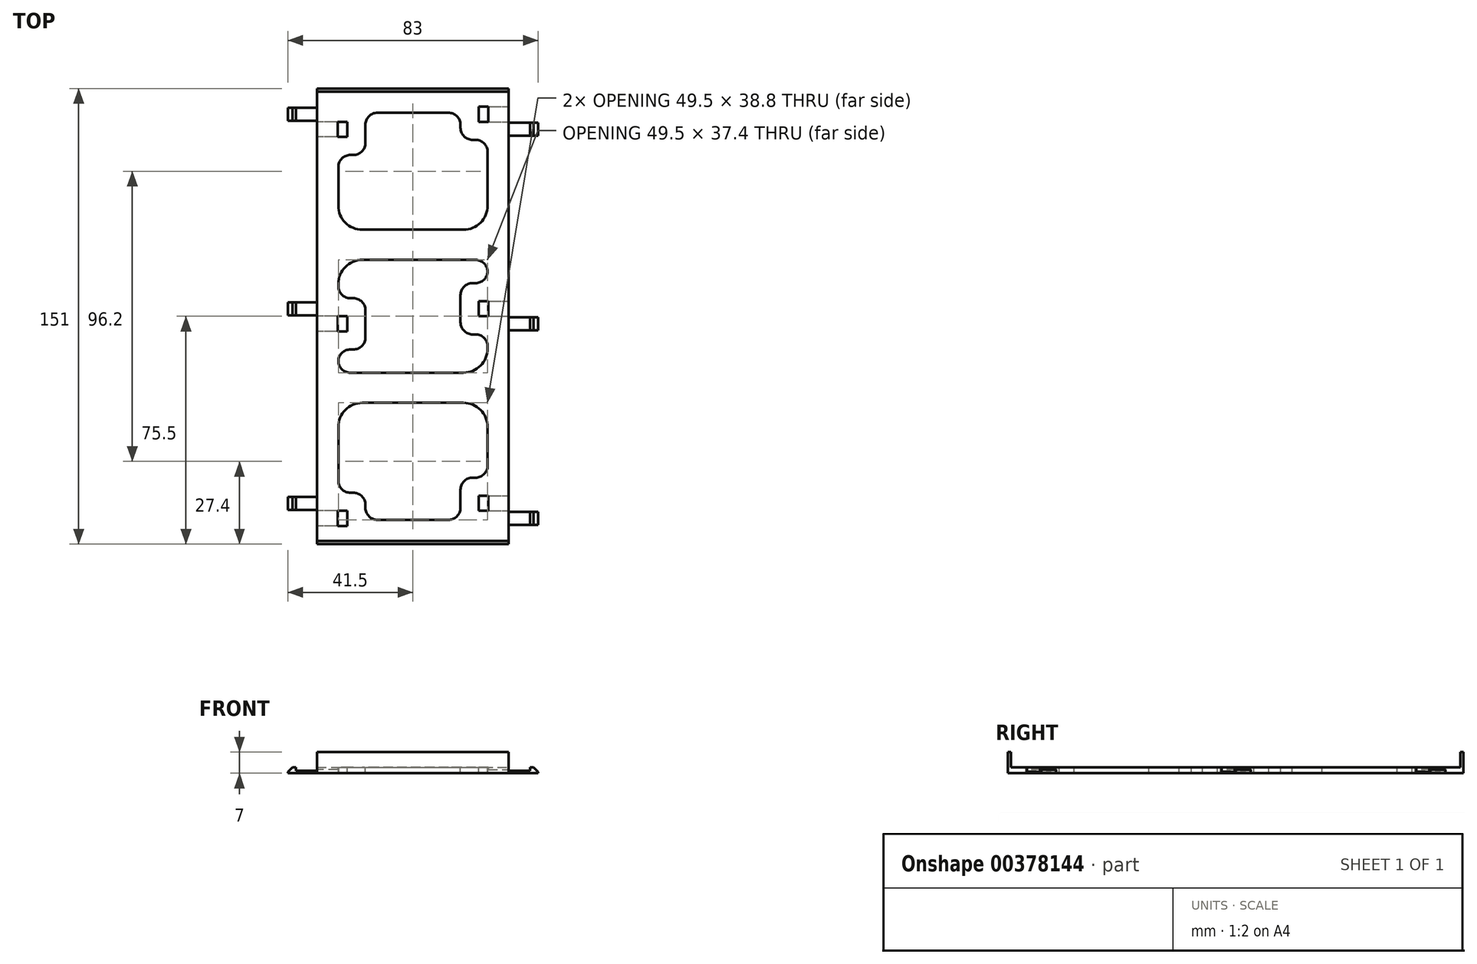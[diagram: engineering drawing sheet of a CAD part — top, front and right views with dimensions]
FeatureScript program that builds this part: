
annotation { "Feature Type Name" : "Feature", "Feature Type Description" : "" }
export const myFeature = defineFeature(function(context is Context, id is Id, definition is map)
    precondition{}
    {
        {
            var Q0;
            Q0=qCreatedBy(makeId("Top.planeOp"),FACE);
            var sketch = newSketch(context, id + "F0", { "sketchPlane" : qUnion([Q0])});
            skLineSegment(sketch, "E0.bottom", {"start": v(0, 0) * mm, "end": v(63.5, 0) * mm});
            skLineSegment(sketch, "E0.top", {"start": v(0, 151) * mm, "end": v(63.5, 151) * mm});
            skLineSegment(sketch, "E0.left", {"start": v(0, 0) * mm, "end": v(0, 151) * mm});
            skLineSegment(sketch, "E0.right", {"start": v(63.5, 0) * mm, "end": v(63.5, 151) * mm});
            skSolve(sketch);
        }
        {
            var Q0;
            Q0=makeQuery(id+"F0.imprint","IMPRINT",FACE,{"disambiguationData":[TD([[makeQuery(id+"F0.imprint","IMPRINT",EDGE,{"derivedFrom":sQuery(id+"F0.wireOp",EDGE,"E0.bottom")}),1.0]])]});
            extrude(context, id + "F1", {"entities" : qUnion([Q0]), "depth" : 2 * mm});
        }
        {
            var Q0;
            Q0=makeQuery(id+"F1.opExtrude","CAP_FACE",FACE,{"disambiguationData":[OSD([sQuery(id+"F0.wireOp",EDGE,"E0.bottom"),sQuery(id+"F0.wireOp",EDGE,"E0.top"),sQuery(id+"F0.wireOp",EDGE,"E0.left"),sQuery(id+"F0.wireOp",EDGE,"E0.right")])],"isStart":false});
            var sketch = newSketch(context, id + "F2", { "sketchPlane" : qUnion([Q0])});
            skLineSegment(sketch, "E1.bottom", {"start": v(0, 151) * mm, "end": v(63.5, 151) * mm});
            skLineSegment(sketch, "E1.top", {"start": v(0, 150) * mm, "end": v(63.5, 150) * mm});
            skLineSegment(sketch, "E1.left", {"start": v(0, 151) * mm, "end": v(0, 150) * mm});
            skLineSegment(sketch, "E1.right", {"start": v(63.5, 151) * mm, "end": v(63.5, 150) * mm});
            skLineSegment(sketch, "E2.bottom", {"start": v(0, 0) * mm, "end": v(63.5, 0) * mm});
            skLineSegment(sketch, "E2.top", {"start": v(0, 1) * mm, "end": v(63.5, 1) * mm});
            skLineSegment(sketch, "E2.left", {"start": v(0, 0) * mm, "end": v(0, 1) * mm});
            skLineSegment(sketch, "E2.right", {"start": v(63.5, 0) * mm, "end": v(63.5, 1) * mm});
            skSolve(sketch);
        }
        {
            var Q0;
            Q0=makeQuery(id+"F2.imprint","IMPRINT",FACE,{"disambiguationData":[TD([[makeQuery(id+"F2.imprint","IMPRINT",EDGE,{"derivedFrom":sQuery(id+"F2.wireOp",EDGE,"E2.bottom")}),1.0]])]});
            var Q1;
            Q1=makeQuery(id+"F2.imprint","IMPRINT",FACE,{"disambiguationData":[TD([[makeQuery(id+"F2.imprint","IMPRINT",EDGE,{"derivedFrom":sQuery(id+"F2.wireOp",EDGE,"E1.bottom")}),-1.0]])]});
            extrude(context, id + "F3", {"entities" : qUnion([Q0, Q1]), "operationType" : NewBodyOperationType.ADD, "depth" : 5 * mm});
        }
        {
            var Q0;
            Q0=makeQuery(id+"F3.boolean.opBoolean","MERGE",FACE,{"derivedFrom":[makeQuery(id+"F1.opExtrude","SWEPT_FACE",FACE,{"disambiguationData":[OSD([sQuery(id+"F0.wireOp",EDGE,"E0.right")])]}),makeQuery(id+"F3.opExtrude","SWEPT_FACE",FACE,{"disambiguationData":[OSD([sQuery(id+"F2.wireOp",EDGE,"E1.right")])]}),makeQuery(id+"F3.opExtrude","SWEPT_FACE",FACE,{"disambiguationData":[OSD([sQuery(id+"F2.wireOp",EDGE,"E2.right")])]})]});
            var sketch = newSketch(context, id + "F4", { "sketchPlane" : qUnion([Q0])});
            skLineSegment(sketch, "E3.bottom", {"start": v(11, 0) * mm, "end": v(16, 0) * mm});
            skLineSegment(sketch, "E3.top", {"start": v(11, 1.2) * mm, "end": v(16, 1.2) * mm});
            skLineSegment(sketch, "E3.left", {"start": v(11, 0) * mm, "end": v(11, 1.2) * mm});
            skLineSegment(sketch, "E3.right", {"start": v(16, 0) * mm, "end": v(16, 1.2) * mm});
            skLineSegment(sketch, "E4.bottom", {"start": v(75.5, 0) * mm, "end": v(80.5, 0) * mm});
            skLineSegment(sketch, "E4.top", {"start": v(75.5, 1.2) * mm, "end": v(80.5, 1.2) * mm});
            skLineSegment(sketch, "E4.left", {"start": v(75.5, 0) * mm, "end": v(75.5, 1.2) * mm});
            skLineSegment(sketch, "E4.right", {"start": v(80.5, 0) * mm, "end": v(80.5, 1.2) * mm});
            skLineSegment(sketch, "E5.bottom", {"start": v(140, 0) * mm, "end": v(145, 0) * mm});
            skLineSegment(sketch, "E5.top", {"start": v(140, 1.2) * mm, "end": v(145, 1.2) * mm});
            skLineSegment(sketch, "E5.left", {"start": v(140, 0) * mm, "end": v(140, 1.2) * mm});
            skLineSegment(sketch, "E5.right", {"start": v(145, 0) * mm, "end": v(145, 1.2) * mm});
            skSolve(sketch);
        }
        {
            var Q0;
            Q0=makeQuery(id+"F4.imprint","IMPRINT",FACE,{"disambiguationData":[TD([[makeQuery(id+"F4.imprint","IMPRINT",EDGE,{"derivedFrom":sQuery(id+"F4.wireOp",EDGE,"E3.bottom")}),1.0]])]});
            var Q1;
            Q1=makeQuery(id+"F4.imprint","IMPRINT",FACE,{"disambiguationData":[TD([[makeQuery(id+"F4.imprint","IMPRINT",EDGE,{"derivedFrom":sQuery(id+"F4.wireOp",EDGE,"E4.bottom")}),1.0]])]});
            var Q2;
            Q2=makeQuery(id+"F4.imprint","IMPRINT",FACE,{"disambiguationData":[TD([[makeQuery(id+"F4.imprint","IMPRINT",EDGE,{"derivedFrom":sQuery(id+"F4.wireOp",EDGE,"E5.bottom")}),1.0]])]});
            extrude(context, id + "F5", {"entities" : qUnion([Q0, Q1, Q2]), "operationType" : NewBodyOperationType.REMOVE, "oppositeDirection" : true, "depth" : 10 * mm});
        }
        {
            var Q0;
            Q0=makeQuery(id+"F3.boolean.opBoolean","MERGE",FACE,{"derivedFrom":[makeQuery(id+"F1.opExtrude","SWEPT_FACE",FACE,{"disambiguationData":[OSD([sQuery(id+"F0.wireOp",EDGE,"E0.left")])]}),makeQuery(id+"F3.opExtrude","SWEPT_FACE",FACE,{"disambiguationData":[OSD([sQuery(id+"F2.wireOp",EDGE,"E1.left")])]}),makeQuery(id+"F3.opExtrude","SWEPT_FACE",FACE,{"disambiguationData":[OSD([sQuery(id+"F2.wireOp",EDGE,"E2.left")])]})]});
            var sketch = newSketch(context, id + "F6", { "sketchPlane" : qUnion([Q0])});
            skLineSegment(sketch, "E6.bottom", {"start": v(-140, 0) * mm, "end": v(-135, 0) * mm});
            skLineSegment(sketch, "E6.top", {"start": v(-140, 1.2) * mm, "end": v(-135, 1.2) * mm});
            skLineSegment(sketch, "E6.left", {"start": v(-140, 0) * mm, "end": v(-140, 1.2) * mm});
            skLineSegment(sketch, "E6.right", {"start": v(-135, 0) * mm, "end": v(-135, 1.2) * mm});
            skLineSegment(sketch, "E7.bottom", {"start": v(-75.5, 0) * mm, "end": v(-70.5, 0) * mm});
            skLineSegment(sketch, "E7.top", {"start": v(-75.5, 1.2) * mm, "end": v(-70.5, 1.2) * mm});
            skLineSegment(sketch, "E7.left", {"start": v(-75.5, 0) * mm, "end": v(-75.5, 1.2) * mm});
            skLineSegment(sketch, "E7.right", {"start": v(-70.5, 0) * mm, "end": v(-70.5, 1.2) * mm});
            skLineSegment(sketch, "E8.bottom", {"start": v(-11, 0) * mm, "end": v(-6, 0) * mm});
            skLineSegment(sketch, "E8.top", {"start": v(-11, 1.2) * mm, "end": v(-6, 1.2) * mm});
            skLineSegment(sketch, "E8.left", {"start": v(-11, 0) * mm, "end": v(-11, 1.2) * mm});
            skLineSegment(sketch, "E8.right", {"start": v(-6, 0) * mm, "end": v(-6, 1.2) * mm});
            skSolve(sketch);
        }
        {
            var Q0;
            Q0=makeQuery(id+"F6.imprint","IMPRINT",FACE,{"disambiguationData":[TD([[makeQuery(id+"F6.imprint","IMPRINT",EDGE,{"derivedFrom":sQuery(id+"F6.wireOp",EDGE,"E6.bottom")}),-1.0]])]});
            var Q1;
            Q1=makeQuery(id+"F6.imprint","IMPRINT",FACE,{"disambiguationData":[TD([[makeQuery(id+"F6.imprint","IMPRINT",EDGE,{"derivedFrom":sQuery(id+"F6.wireOp",EDGE,"E7.bottom")}),-1.0]])]});
            var Q2;
            Q2=makeQuery(id+"F6.imprint","IMPRINT",FACE,{"disambiguationData":[TD([[makeQuery(id+"F6.imprint","IMPRINT",EDGE,{"derivedFrom":sQuery(id+"F6.wireOp",EDGE,"E8.bottom")}),-1.0]])]});
            extrude(context, id + "F7", {"entities" : qUnion([Q0, Q1, Q2]), "operationType" : NewBodyOperationType.REMOVE, "oppositeDirection" : true, "depth" : 10 * mm});
        }
        {
            var Q0;
            Q0=makeQuery(id+"F3.boolean.opBoolean","MERGE",FACE,{"derivedFrom":[makeQuery(id+"F1.opExtrude","SWEPT_FACE",FACE,{"disambiguationData":[OSD([sQuery(id+"F0.wireOp",EDGE,"E0.right")])]}),makeQuery(id+"F3.opExtrude","SWEPT_FACE",FACE,{"disambiguationData":[OSD([sQuery(id+"F2.wireOp",EDGE,"E1.right")])]}),makeQuery(id+"F3.opExtrude","SWEPT_FACE",FACE,{"disambiguationData":[OSD([sQuery(id+"F2.wireOp",EDGE,"E2.right")])]})]});
            var sketch = newSketch(context, id + "F8", { "sketchPlane" : qUnion([Q0])});
            skLineSegment(sketch, "E9.bottom", {"start": v(6.35, 0.8) * mm, "end": v(10.65, 0.8) * mm});
            skLineSegment(sketch, "E9.top", {"start": v(6.35, 0) * mm, "end": v(10.65, 0) * mm});
            skLineSegment(sketch, "E9.left", {"start": v(6.35, 0.8) * mm, "end": v(6.35, 0) * mm});
            skLineSegment(sketch, "E9.right", {"start": v(10.65, 0.8) * mm, "end": v(10.65, 0) * mm});
            skLineSegment(sketch, "E10.bottom", {"start": v(70.85, 0.8) * mm, "end": v(75.15, 0.8) * mm});
            skLineSegment(sketch, "E10.top", {"start": v(70.85, 0) * mm, "end": v(75.15, 0) * mm});
            skLineSegment(sketch, "E10.left", {"start": v(70.85, 0.8) * mm, "end": v(70.85, 0) * mm});
            skLineSegment(sketch, "E10.right", {"start": v(75.15, 0.8) * mm, "end": v(75.15, 0) * mm});
            skLineSegment(sketch, "E11.bottom", {"start": v(135.35, 0.8) * mm, "end": v(139.65, 0.8) * mm});
            skLineSegment(sketch, "E11.top", {"start": v(135.35, 0) * mm, "end": v(139.65, 0) * mm});
            skLineSegment(sketch, "E11.left", {"start": v(135.35, 0.8) * mm, "end": v(135.35, 0) * mm});
            skLineSegment(sketch, "E11.right", {"start": v(139.65, 0.8) * mm, "end": v(139.65, 0) * mm});
            skSolve(sketch);
        }
        {
            var Q0;
            Q0=makeQuery(id+"F8.imprint","IMPRINT",FACE,{"disambiguationData":[TD([[makeQuery(id+"F8.imprint","IMPRINT",EDGE,{"derivedFrom":sQuery(id+"F8.wireOp",EDGE,"E11.bottom")}),-1.0]])]});
            var Q1;
            Q1=makeQuery(id+"F8.imprint","IMPRINT",FACE,{"disambiguationData":[TD([[makeQuery(id+"F8.imprint","IMPRINT",EDGE,{"derivedFrom":sQuery(id+"F8.wireOp",EDGE,"E10.bottom")}),-1.0]])]});
            var Q2;
            Q2=makeQuery(id+"F8.imprint","IMPRINT",FACE,{"disambiguationData":[TD([[makeQuery(id+"F8.imprint","IMPRINT",EDGE,{"derivedFrom":sQuery(id+"F8.wireOp",EDGE,"E9.bottom")}),-1.0]])]});
            extrude(context, id + "F9", {"entities" : qUnion([Q0, Q1, Q2]), "operationType" : NewBodyOperationType.ADD, "depth" : 9.75 * mm});
        }
        {
            var Q0;
            Q0=makeQuery(id+"F3.boolean.opBoolean","MERGE",FACE,{"derivedFrom":[makeQuery(id+"F1.opExtrude","SWEPT_FACE",FACE,{"disambiguationData":[OSD([sQuery(id+"F0.wireOp",EDGE,"E0.left")])]}),makeQuery(id+"F3.opExtrude","SWEPT_FACE",FACE,{"disambiguationData":[OSD([sQuery(id+"F2.wireOp",EDGE,"E1.left")])]}),makeQuery(id+"F3.opExtrude","SWEPT_FACE",FACE,{"disambiguationData":[OSD([sQuery(id+"F2.wireOp",EDGE,"E2.left")])]})]});
            var sketch = newSketch(context, id + "F10", { "sketchPlane" : qUnion([Q0])});
            skPoint(sketch, "E12.firstSnap0", {"position": v(-144.65, 0) * mm});
            skLineSegment(sketch, "E12.bottom", {"start": v(-144.65, 0.8) * mm, "end": v(-140.35, 0.8) * mm});
            skLineSegment(sketch, "E12.top", {"start": v(-144.65, 0) * mm, "end": v(-140.35, 0) * mm});
            skLineSegment(sketch, "E12.left", {"start": v(-144.65, 0.8) * mm, "end": v(-144.65, 0) * mm});
            skLineSegment(sketch, "E12.right", {"start": v(-140.35, 0.8) * mm, "end": v(-140.35, 0) * mm});
            skLineSegment(sketch, "E13.bottom", {"start": v(-80.15, 0.8) * mm, "end": v(-75.85, 0.8) * mm});
            skLineSegment(sketch, "E13.top", {"start": v(-80.15, 0) * mm, "end": v(-75.85, 0) * mm});
            skLineSegment(sketch, "E13.left", {"start": v(-80.15, 0.8) * mm, "end": v(-80.15, 0) * mm});
            skLineSegment(sketch, "E13.right", {"start": v(-75.85, 0.8) * mm, "end": v(-75.85, 0) * mm});
            skLineSegment(sketch, "E14.bottom", {"start": v(-15.65, 0.8) * mm, "end": v(-11.35, 0.8) * mm});
            skLineSegment(sketch, "E14.top", {"start": v(-15.65, 0) * mm, "end": v(-11.35, 0) * mm});
            skLineSegment(sketch, "E14.left", {"start": v(-15.65, 0.8) * mm, "end": v(-15.65, 0) * mm});
            skLineSegment(sketch, "E14.right", {"start": v(-11.35, 0.8) * mm, "end": v(-11.35, 0) * mm});
            skSolve(sketch);
        }
        {
            var Q0;
            Q0=makeQuery(id+"F10.imprint","IMPRINT",FACE,{"disambiguationData":[TD([[makeQuery(id+"F10.imprint","IMPRINT",EDGE,{"derivedFrom":sQuery(id+"F10.wireOp",EDGE,"E14.bottom")}),-1.0]])]});
            var Q1;
            Q1=makeQuery(id+"F10.imprint","IMPRINT",FACE,{"disambiguationData":[TD([[makeQuery(id+"F10.imprint","IMPRINT",EDGE,{"derivedFrom":sQuery(id+"F10.wireOp",EDGE,"E13.bottom")}),-1.0]])]});
            var Q2;
            Q2=makeQuery(id+"F10.imprint","IMPRINT",FACE,{"disambiguationData":[TD([[makeQuery(id+"F10.imprint","IMPRINT",EDGE,{"derivedFrom":sQuery(id+"F10.wireOp",EDGE,"E12.bottom")}),-1.0]])]});
            extrude(context, id + "F11", {"entities" : qUnion([Q0, Q1, Q2]), "operationType" : NewBodyOperationType.ADD, "depth" : 9.75 * mm});
        }
        {
            var Q0;
            Q0=makeQuery(id+"F9.opExtrude","SWEPT_FACE",FACE,{"disambiguationData":[OSD([sQuery(id+"F8.wireOp",EDGE,"E9.bottom")])]});
            var sketch = newSketch(context, id + "F12", { "sketchPlane" : qUnion([Q0])});
            skLineSegment(sketch, "E15.bottom", {"start": v(73.25, 6.35) * mm, "end": v(70.5, 6.35) * mm});
            skLineSegment(sketch, "E15.top", {"start": v(73.25, 10.65) * mm, "end": v(70.5, 10.65) * mm});
            skLineSegment(sketch, "E15.left", {"start": v(73.25, 6.35) * mm, "end": v(73.25, 10.65) * mm});
            skLineSegment(sketch, "E15.right", {"start": v(70.5, 6.35) * mm, "end": v(70.5, 10.65) * mm});
            skSolve(sketch);
        }
        {
            var Q0;
            Q0=makeQuery(id+"F12.imprint","IMPRINT",FACE,{"disambiguationData":[TD([[makeQuery(id+"F12.imprint","IMPRINT",EDGE,{"derivedFrom":sQuery(id+"F12.wireOp",EDGE,"E15.bottom")}),-1.0]])]});
            extrude(context, id + "F13", {"entities" : qUnion([Q0]), "operationType" : NewBodyOperationType.ADD, "depth" : 1.2 * mm});
        }
        {
            var Q0;
            Q0=makeQuery(id+"F11.opExtrude","SWEPT_FACE",FACE,{"disambiguationData":[OSD([sQuery(id+"F10.wireOp",EDGE,"E14.bottom")])]});
            var sketch = newSketch(context, id + "F14", { "sketchPlane" : qUnion([Q0])});
            skLineSegment(sketch, "E16.bottom", {"start": v(-9.75, 15.65) * mm, "end": v(-7, 15.65) * mm});
            skLineSegment(sketch, "E16.top", {"start": v(-9.75, 11.35) * mm, "end": v(-7, 11.35) * mm});
            skLineSegment(sketch, "E16.left", {"start": v(-9.75, 15.65) * mm, "end": v(-9.75, 11.35) * mm});
            skLineSegment(sketch, "E16.right", {"start": v(-7, 15.65) * mm, "end": v(-7, 11.35) * mm});
            skSolve(sketch);
        }
        {
            var Q0;
            Q0=makeQuery(id+"F14.imprint","IMPRINT",FACE,{"disambiguationData":[TD([[makeQuery(id+"F14.imprint","IMPRINT",EDGE,{"derivedFrom":sQuery(id+"F14.wireOp",EDGE,"E16.bottom")}),-1.0]])]});
            extrude(context, id + "F15", {"entities" : qUnion([Q0]), "operationType" : NewBodyOperationType.ADD, "depth" : 1.2 * mm});
        }
        {
            var Q0;
            Q0=makeQuery(id+"F9.opExtrude","SWEPT_FACE",FACE,{"disambiguationData":[OSD([sQuery(id+"F8.wireOp",EDGE,"E10.bottom")])]});
            var sketch = newSketch(context, id + "F16", { "sketchPlane" : qUnion([Q0])});
            skLineSegment(sketch, "E17.bottom", {"start": v(73.25, 75.15) * mm, "end": v(70.5, 75.15) * mm});
            skLineSegment(sketch, "E17.top", {"start": v(73.25, 70.85) * mm, "end": v(70.5, 70.85) * mm});
            skLineSegment(sketch, "E17.left", {"start": v(73.25, 75.15) * mm, "end": v(73.25, 70.85) * mm});
            skLineSegment(sketch, "E17.right", {"start": v(70.5, 75.15) * mm, "end": v(70.5, 70.85) * mm});
            skSolve(sketch);
        }
        {
            var Q0;
            Q0=makeQuery(id+"F16.imprint","IMPRINT",FACE,{"disambiguationData":[TD([[makeQuery(id+"F16.imprint","IMPRINT",EDGE,{"derivedFrom":sQuery(id+"F16.wireOp",EDGE,"E17.bottom")}),1.0]])]});
            extrude(context, id + "F17", {"entities" : qUnion([Q0]), "operationType" : NewBodyOperationType.ADD, "depth" : 1.2 * mm});
        }
        {
            var Q0;
            Q0=makeQuery(id+"F11.opExtrude","SWEPT_FACE",FACE,{"disambiguationData":[OSD([sQuery(id+"F10.wireOp",EDGE,"E13.bottom")])]});
            var sketch = newSketch(context, id + "F18", { "sketchPlane" : qUnion([Q0])});
            skLineSegment(sketch, "E18.bottom", {"start": v(-9.75, 80.15) * mm, "end": v(-7, 80.15) * mm});
            skLineSegment(sketch, "E18.top", {"start": v(-9.75, 75.85) * mm, "end": v(-7, 75.85) * mm});
            skLineSegment(sketch, "E18.left", {"start": v(-9.75, 80.15) * mm, "end": v(-9.75, 75.85) * mm});
            skLineSegment(sketch, "E18.right", {"start": v(-7, 80.15) * mm, "end": v(-7, 75.85) * mm});
            skSolve(sketch);
        }
        {
            var Q0;
            Q0=makeQuery(id+"F18.imprint","IMPRINT",FACE,{"disambiguationData":[TD([[makeQuery(id+"F18.imprint","IMPRINT",EDGE,{"derivedFrom":sQuery(id+"F18.wireOp",EDGE,"E18.bottom")}),-1.0]])]});
            extrude(context, id + "F19", {"entities" : qUnion([Q0]), "operationType" : NewBodyOperationType.ADD, "depth" : 1.2 * mm});
        }
        {
            var Q0;
            Q0=makeQuery(id+"F9.opExtrude","SWEPT_FACE",FACE,{"disambiguationData":[OSD([sQuery(id+"F8.wireOp",EDGE,"E11.bottom")])]});
            var sketch = newSketch(context, id + "F20", { "sketchPlane" : qUnion([Q0])});
            skLineSegment(sketch, "E19.bottom", {"start": v(73.25, 139.65) * mm, "end": v(70.5, 139.65) * mm});
            skLineSegment(sketch, "E19.top", {"start": v(73.25, 135.35) * mm, "end": v(70.5, 135.35) * mm});
            skLineSegment(sketch, "E19.left", {"start": v(73.25, 139.65) * mm, "end": v(73.25, 135.35) * mm});
            skLineSegment(sketch, "E19.right", {"start": v(70.5, 139.65) * mm, "end": v(70.5, 135.35) * mm});
            skSolve(sketch);
        }
        {
            var Q0;
            Q0=makeQuery(id+"F20.imprint","IMPRINT",FACE,{"disambiguationData":[TD([[makeQuery(id+"F20.imprint","IMPRINT",EDGE,{"derivedFrom":sQuery(id+"F20.wireOp",EDGE,"E19.bottom")}),1.0]])]});
            extrude(context, id + "F21", {"entities" : qUnion([Q0]), "operationType" : NewBodyOperationType.ADD, "depth" : 1.2 * mm});
        }
        {
            var Q0;
            Q0=makeQuery(id+"F11.opExtrude","SWEPT_FACE",FACE,{"disambiguationData":[OSD([sQuery(id+"F10.wireOp",EDGE,"E12.bottom")])]});
            var sketch = newSketch(context, id + "F22", { "sketchPlane" : qUnion([Q0])});
            skLineSegment(sketch, "E20.bottom", {"start": v(-9.75, 144.65) * mm, "end": v(-7, 144.65) * mm});
            skLineSegment(sketch, "E20.top", {"start": v(-9.75, 140.35) * mm, "end": v(-7, 140.35) * mm});
            skLineSegment(sketch, "E20.left", {"start": v(-9.75, 144.65) * mm, "end": v(-9.75, 140.35) * mm});
            skLineSegment(sketch, "E20.right", {"start": v(-7, 144.65) * mm, "end": v(-7, 140.35) * mm});
            skSolve(sketch);
        }
        {
            var Q0;
            Q0=makeQuery(id+"F22.imprint","IMPRINT",FACE,{"disambiguationData":[TD([[makeQuery(id+"F22.imprint","IMPRINT",EDGE,{"derivedFrom":sQuery(id+"F22.wireOp",EDGE,"E20.bottom")}),-1.0]])]});
            extrude(context, id + "F23", {"entities" : qUnion([Q0]), "operationType" : NewBodyOperationType.ADD, "depth" : 1.2 * mm});
        }
        {
            var Q0;
            Q0=makeQuery(id+"F5.boolean.opBoolean","COPY",FACE,{"derivedFrom":makeQuery(id+"F5.opExtrude","SWEPT_FACE",FACE,{"disambiguationData":[OSD([sQuery(id+"F4.wireOp",EDGE,"E5.top")])]})});
            var sketch = newSketch(context, id + "F24", { "sketchPlane" : qUnion([Q0])});
            skLineSegment(sketch, "E21.bottom", {"start": v(53.5, -145) * mm, "end": v(56.75, -145) * mm});
            skLineSegment(sketch, "E21.top", {"start": v(53.5, -140) * mm, "end": v(56.75, -140) * mm});
            skLineSegment(sketch, "E21.left", {"start": v(53.5, -145) * mm, "end": v(53.5, -140) * mm});
            skLineSegment(sketch, "E21.right", {"start": v(56.75, -145) * mm, "end": v(56.75, -140) * mm});
            skSolve(sketch);
        }
        {
            var Q0;
            Q0=makeQuery(id+"F7.boolean.opBoolean","COPY",FACE,{"derivedFrom":makeQuery(id+"F7.opExtrude","SWEPT_FACE",FACE,{"disambiguationData":[OSD([sQuery(id+"F6.wireOp",EDGE,"E6.top")])]})});
            var sketch = newSketch(context, id + "F25", { "sketchPlane" : qUnion([Q0])});
            skLineSegment(sketch, "E22.bottom", {"start": v(10, -140) * mm, "end": v(6.75, -140) * mm});
            skLineSegment(sketch, "E22.top", {"start": v(10, -135) * mm, "end": v(6.75, -135) * mm});
            skLineSegment(sketch, "E22.left", {"start": v(10, -140) * mm, "end": v(10, -135) * mm});
            skLineSegment(sketch, "E22.right", {"start": v(6.75, -140) * mm, "end": v(6.75, -135) * mm});
            skSolve(sketch);
        }
        {
            var Q0;
            Q0=makeQuery(id+"F5.boolean.opBoolean","COPY",FACE,{"derivedFrom":makeQuery(id+"F5.opExtrude","SWEPT_FACE",FACE,{"disambiguationData":[OSD([sQuery(id+"F4.wireOp",EDGE,"E4.top")])]})});
            var sketch = newSketch(context, id + "F26", { "sketchPlane" : qUnion([Q0])});
            skLineSegment(sketch, "E23.bottom", {"start": v(53.5, -80.5) * mm, "end": v(56.75, -80.5) * mm});
            skLineSegment(sketch, "E23.top", {"start": v(53.5, -75.5) * mm, "end": v(56.75, -75.5) * mm});
            skLineSegment(sketch, "E23.left", {"start": v(53.5, -80.5) * mm, "end": v(53.5, -75.5) * mm});
            skLineSegment(sketch, "E23.right", {"start": v(56.75, -80.5) * mm, "end": v(56.75, -75.5) * mm});
            skSolve(sketch);
        }
        {
            var Q0;
            Q0=makeQuery(id+"F7.boolean.opBoolean","COPY",FACE,{"derivedFrom":makeQuery(id+"F7.opExtrude","SWEPT_FACE",FACE,{"disambiguationData":[OSD([sQuery(id+"F6.wireOp",EDGE,"E7.top")])]})});
            var sketch = newSketch(context, id + "F27", { "sketchPlane" : qUnion([Q0])});
            skLineSegment(sketch, "E24.bottom", {"start": v(10, -75.5) * mm, "end": v(6.75, -75.5) * mm});
            skLineSegment(sketch, "E24.top", {"start": v(10, -70.5) * mm, "end": v(6.75, -70.5) * mm});
            skLineSegment(sketch, "E24.left", {"start": v(10, -75.5) * mm, "end": v(10, -70.5) * mm});
            skLineSegment(sketch, "E24.right", {"start": v(6.75, -75.5) * mm, "end": v(6.75, -70.5) * mm});
            skSolve(sketch);
        }
        {
            var Q0;
            Q0=makeQuery(id+"F5.boolean.opBoolean","COPY",FACE,{"derivedFrom":makeQuery(id+"F5.opExtrude","SWEPT_FACE",FACE,{"disambiguationData":[OSD([sQuery(id+"F4.wireOp",EDGE,"E3.top")])]})});
            var sketch = newSketch(context, id + "F28", { "sketchPlane" : qUnion([Q0])});
            skLineSegment(sketch, "E25.bottom", {"start": v(53.5, -16) * mm, "end": v(56.75, -16) * mm});
            skLineSegment(sketch, "E25.top", {"start": v(53.5, -11) * mm, "end": v(56.75, -11) * mm});
            skLineSegment(sketch, "E25.left", {"start": v(53.5, -16) * mm, "end": v(53.5, -11) * mm});
            skLineSegment(sketch, "E25.right", {"start": v(56.75, -16) * mm, "end": v(56.75, -11) * mm});
            skSolve(sketch);
        }
        {
            var Q0;
            Q0=makeQuery(id+"F7.boolean.opBoolean","COPY",FACE,{"derivedFrom":makeQuery(id+"F7.opExtrude","SWEPT_FACE",FACE,{"disambiguationData":[OSD([sQuery(id+"F6.wireOp",EDGE,"E8.top")])]})});
            var sketch = newSketch(context, id + "F29", { "sketchPlane" : qUnion([Q0])});
            skLineSegment(sketch, "E26.bottom", {"start": v(10, -11) * mm, "end": v(6.75, -11) * mm});
            skLineSegment(sketch, "E26.top", {"start": v(10, -6) * mm, "end": v(6.75, -6) * mm});
            skLineSegment(sketch, "E26.left", {"start": v(10, -11) * mm, "end": v(10, -6) * mm});
            skLineSegment(sketch, "E26.right", {"start": v(6.75, -11) * mm, "end": v(6.75, -6) * mm});
            skSolve(sketch);
        }
        {
            var Q0;
            Q0=makeQuery(id+"F28.imprint","IMPRINT",FACE,{"disambiguationData":[TD([[makeQuery(id+"F28.imprint","IMPRINT",EDGE,{"derivedFrom":sQuery(id+"F28.wireOp",EDGE,"E25.bottom")}),1.0]])]});
            var Q1;
            Q1=makeQuery(id+"F29.imprint","IMPRINT",FACE,{"disambiguationData":[TD([[makeQuery(id+"F29.imprint","IMPRINT",EDGE,{"derivedFrom":sQuery(id+"F29.wireOp",EDGE,"E26.bottom")}),-1.0]])]});
            var Q2;
            Q2=makeQuery(id+"F27.imprint","IMPRINT",FACE,{"disambiguationData":[TD([[makeQuery(id+"F27.imprint","IMPRINT",EDGE,{"derivedFrom":sQuery(id+"F27.wireOp",EDGE,"E24.bottom")}),-1.0]])]});
            var Q3;
            Q3=makeQuery(id+"F26.imprint","IMPRINT",FACE,{"disambiguationData":[TD([[makeQuery(id+"F26.imprint","IMPRINT",EDGE,{"derivedFrom":sQuery(id+"F26.wireOp",EDGE,"E23.bottom")}),1.0]])]});
            var Q4;
            Q4=makeQuery(id+"F25.imprint","IMPRINT",FACE,{"disambiguationData":[TD([[makeQuery(id+"F25.imprint","IMPRINT",EDGE,{"derivedFrom":sQuery(id+"F25.wireOp",EDGE,"E22.bottom")}),-1.0]])]});
            var Q5;
            Q5=makeQuery(id+"F24.imprint","IMPRINT",FACE,{"disambiguationData":[TD([[makeQuery(id+"F24.imprint","IMPRINT",EDGE,{"derivedFrom":sQuery(id+"F24.wireOp",EDGE,"E21.bottom")}),1.0]])]});
            extrude(context, id + "F30", {"entities" : qUnion([Q0, Q1, Q2, Q3, Q4, Q5]), "operationType" : NewBodyOperationType.REMOVE, "endBound" : BoundingType.THROUGH_ALL, "oppositeDirection" : true, "depth" : 25 * mm});
        }
        {
            var Q0;
            Q0=makeQuery(id+"F13.opExtrude","CAP_EDGE",EDGE,{"disambiguationData":[OSD([sQuery(id+"F12.wireOp",EDGE,"E15.left")])],"isStart":false});
            var Q1;
            Q1=makeQuery(id+"F17.opExtrude","CAP_EDGE",EDGE,{"disambiguationData":[OSD([sQuery(id+"F16.wireOp",EDGE,"E17.left")])],"isStart":false});
            var Q2;
            Q2=makeQuery(id+"F21.opExtrude","CAP_EDGE",EDGE,{"disambiguationData":[OSD([sQuery(id+"F20.wireOp",EDGE,"E19.left")])],"isStart":false});
            var Q3;
            Q3=makeQuery(id+"F23.opExtrude","CAP_EDGE",EDGE,{"disambiguationData":[OSD([sQuery(id+"F22.wireOp",EDGE,"E20.left")])],"isStart":false});
            var Q4;
            Q4=makeQuery(id+"F19.opExtrude","CAP_EDGE",EDGE,{"disambiguationData":[OSD([sQuery(id+"F18.wireOp",EDGE,"E18.left")])],"isStart":false});
            var Q5;
            Q5=makeQuery(id+"F15.opExtrude","CAP_EDGE",EDGE,{"disambiguationData":[OSD([sQuery(id+"F14.wireOp",EDGE,"E16.left")])],"isStart":false});
            chamfer(context, id + "F31", {"entities" : qUnion([Q0, Q1, Q2, Q3, Q4, Q5]), "width" : 1.6 * mm, "tangentPropagation" : true});
        }
        {
            var Q0;
            Q0=makeQuery(id+"F1.opExtrude","CAP_FACE",FACE,{"disambiguationData":[OSD([sQuery(id+"F0.wireOp",EDGE,"E0.bottom"),sQuery(id+"F0.wireOp",EDGE,"E0.top"),sQuery(id+"F0.wireOp",EDGE,"E0.left"),sQuery(id+"F0.wireOp",EDGE,"E0.right")])],"isStart":false});
            var sketch = newSketch(context, id + "F32", { "sketchPlane" : qUnion([Q0])});
            skLineSegment(sketch, "E27", {"start": v(7, 17) * mm, "end": v(7, 46.8) * mm});
            skLineSegment(sketch, "E28", {"start": v(7, 46.8) * mm, "end": v(56.5, 46.8) * mm});
            skLineSegment(sketch, "E29", {"start": v(56.5, 46.8) * mm, "end": v(56.5, 22) * mm});
            skLineSegment(sketch, "E30", {"start": v(56.5, 22) * mm, "end": v(47.5, 22) * mm});
            skLineSegment(sketch, "E31", {"start": v(47.5, 22) * mm, "end": v(47.5, 8) * mm});
            skLineSegment(sketch, "E32", {"start": v(47.5, 8) * mm, "end": v(16, 8) * mm});
            skLineSegment(sketch, "E33", {"start": v(16, 8) * mm, "end": v(16, 17) * mm});
            skLineSegment(sketch, "E34", {"start": v(16, 17) * mm, "end": v(7, 17) * mm});
            skLineSegment(sketch, "E35", {"start": v(7, 56.8) * mm, "end": v(56.5, 56.8) * mm});
            skLineSegment(sketch, "E36", {"start": v(56.5, 56.8) * mm, "end": v(56.5, 69.5) * mm});
            skLineSegment(sketch, "E37", {"start": v(56.5, 69.5) * mm, "end": v(47.5, 69.5) * mm});
            skLineSegment(sketch, "E38", {"start": v(47.5, 69.5) * mm, "end": v(47.5, 86.5) * mm});
            skLineSegment(sketch, "E39", {"start": v(47.5, 86.5) * mm, "end": v(56.5, 86.5) * mm});
            skLineSegment(sketch, "E40", {"start": v(56.5, 86.5) * mm, "end": v(56.5, 94.2) * mm});
            skLineSegment(sketch, "E41", {"start": v(56.5, 94.2) * mm, "end": v(7, 94.2) * mm});
            skLineSegment(sketch, "E42", {"start": v(7, 94.2) * mm, "end": v(7, 81.5) * mm});
            skLineSegment(sketch, "E43", {"start": v(7, 81.5) * mm, "end": v(16, 81.5) * mm});
            skLineSegment(sketch, "E44", {"start": v(16, 81.5) * mm, "end": v(16, 64.5) * mm});
            skLineSegment(sketch, "E45", {"start": v(16, 64.5) * mm, "end": v(7, 64.5) * mm});
            skLineSegment(sketch, "E46", {"start": v(7, 64.5) * mm, "end": v(7, 56.8) * mm});
            skLineSegment(sketch, "E47", {"start": v(7, 104.2) * mm, "end": v(56.5, 104.2) * mm});
            skLineSegment(sketch, "E48", {"start": v(56.5, 104.2) * mm, "end": v(56.5, 134) * mm});
            skLineSegment(sketch, "E49", {"start": v(56.5, 134) * mm, "end": v(47.5, 134) * mm});
            skLineSegment(sketch, "E50", {"start": v(47.5, 134) * mm, "end": v(47.5, 143) * mm});
            skLineSegment(sketch, "E51", {"start": v(47.5, 143) * mm, "end": v(16, 143) * mm});
            skLineSegment(sketch, "E52", {"start": v(16, 143) * mm, "end": v(16, 129) * mm});
            skLineSegment(sketch, "E53", {"start": v(16, 129) * mm, "end": v(7, 129) * mm});
            skLineSegment(sketch, "E54", {"start": v(7, 129) * mm, "end": v(7, 104.2) * mm});
            skSolve(sketch);
        }
        {
            var Q0;
            Q0=makeQuery(id+"F32.imprint","IMPRINT",FACE,{"disambiguationData":[TD([[makeQuery(id+"F32.imprint","IMPRINT",EDGE,{"derivedFrom":sQuery(id+"F32.wireOp",EDGE,"E47")}),1.0]])]});
            var Q1;
            Q1=makeQuery(id+"F32.imprint","IMPRINT",FACE,{"disambiguationData":[TD([[makeQuery(id+"F32.imprint","IMPRINT",EDGE,{"derivedFrom":sQuery(id+"F32.wireOp",EDGE,"E35")}),1.0]])]});
            var Q2;
            Q2=makeQuery(id+"F32.imprint","IMPRINT",FACE,{"disambiguationData":[TD([[makeQuery(id+"F32.imprint","IMPRINT",EDGE,{"derivedFrom":sQuery(id+"F32.wireOp",EDGE,"E27")}),-1.0]])]});
            extrude(context, id + "F33", {"entities" : qUnion([Q0, Q1, Q2]), "operationType" : NewBodyOperationType.REMOVE, "endBound" : BoundingType.THROUGH_ALL, "oppositeDirection" : true, "depth" : 25 * mm});
        }
        {
            var Q0;
            Q0=makeQuery(id+"F33.boolean.opBoolean","COPY",EDGE,{"derivedFrom":makeQuery(id+"F33.opExtrude","SWEPT_EDGE",EDGE,{"disambiguationData":[OSD([sQuery(id+"F32.wireOp",EDGE,"E51"),sQuery(id+"F32.wireOp",EDGE,"E52")])]})});
            var Q1;
            Q1=makeQuery(id+"F33.boolean.opBoolean","COPY",EDGE,{"derivedFrom":makeQuery(id+"F33.opExtrude","SWEPT_EDGE",EDGE,{"disambiguationData":[OSD([sQuery(id+"F32.wireOp",EDGE,"E52"),sQuery(id+"F32.wireOp",EDGE,"E53")])]})});
            var Q2;
            Q2=makeQuery(id+"F33.boolean.opBoolean","COPY",EDGE,{"derivedFrom":makeQuery(id+"F33.opExtrude","SWEPT_EDGE",EDGE,{"disambiguationData":[OSD([sQuery(id+"F32.wireOp",EDGE,"E53"),sQuery(id+"F32.wireOp",EDGE,"E54")])]})});
            var Q3;
            Q3=makeQuery(id+"F33.boolean.opBoolean","COPY",EDGE,{"derivedFrom":makeQuery(id+"F33.opExtrude","SWEPT_EDGE",EDGE,{"disambiguationData":[OSD([sQuery(id+"F32.wireOp",EDGE,"E49"),sQuery(id+"F32.wireOp",EDGE,"E50")])]})});
            var Q4;
            Q4=makeQuery(id+"F33.boolean.opBoolean","COPY",EDGE,{"derivedFrom":makeQuery(id+"F33.opExtrude","SWEPT_EDGE",EDGE,{"disambiguationData":[OSD([sQuery(id+"F32.wireOp",EDGE,"E37"),sQuery(id+"F32.wireOp",EDGE,"E38")])]})});
            var Q5;
            Q5=makeQuery(id+"F33.boolean.opBoolean","COPY",EDGE,{"derivedFrom":makeQuery(id+"F33.opExtrude","SWEPT_EDGE",EDGE,{"disambiguationData":[OSD([sQuery(id+"F32.wireOp",EDGE,"E43"),sQuery(id+"F32.wireOp",EDGE,"E44")])]})});
            var Q6;
            Q6=makeQuery(id+"F33.boolean.opBoolean","COPY",EDGE,{"derivedFrom":makeQuery(id+"F33.opExtrude","SWEPT_EDGE",EDGE,{"disambiguationData":[OSD([sQuery(id+"F32.wireOp",EDGE,"E44"),sQuery(id+"F32.wireOp",EDGE,"E45")])]})});
            var Q7;
            Q7=makeQuery(id+"F33.boolean.opBoolean","COPY",EDGE,{"derivedFrom":makeQuery(id+"F33.opExtrude","SWEPT_EDGE",EDGE,{"disambiguationData":[OSD([sQuery(id+"F32.wireOp",EDGE,"E45"),sQuery(id+"F32.wireOp",EDGE,"E46")])]})});
            var Q8;
            Q8=makeQuery(id+"F33.boolean.opBoolean","COPY",EDGE,{"derivedFrom":makeQuery(id+"F33.opExtrude","SWEPT_EDGE",EDGE,{"disambiguationData":[OSD([sQuery(id+"F32.wireOp",EDGE,"E33"),sQuery(id+"F32.wireOp",EDGE,"E34")])]})});
            var Q9;
            Q9=makeQuery(id+"F33.boolean.opBoolean","COPY",EDGE,{"derivedFrom":makeQuery(id+"F33.opExtrude","SWEPT_EDGE",EDGE,{"disambiguationData":[OSD([sQuery(id+"F32.wireOp",EDGE,"E39"),sQuery(id+"F32.wireOp",EDGE,"E40")])]})});
            var Q10;
            Q10=makeQuery(id+"F33.boolean.opBoolean","COPY",EDGE,{"derivedFrom":makeQuery(id+"F33.opExtrude","SWEPT_EDGE",EDGE,{"disambiguationData":[OSD([sQuery(id+"F32.wireOp",EDGE,"E38"),sQuery(id+"F32.wireOp",EDGE,"E39")])]})});
            var Q11;
            Q11=makeQuery(id+"F33.boolean.opBoolean","COPY",EDGE,{"derivedFrom":makeQuery(id+"F33.opExtrude","SWEPT_EDGE",EDGE,{"disambiguationData":[OSD([sQuery(id+"F32.wireOp",EDGE,"E29"),sQuery(id+"F32.wireOp",EDGE,"E30")])]})});
            var Q12;
            Q12=makeQuery(id+"F33.boolean.opBoolean","COPY",EDGE,{"derivedFrom":makeQuery(id+"F33.opExtrude","SWEPT_EDGE",EDGE,{"disambiguationData":[OSD([sQuery(id+"F32.wireOp",EDGE,"E30"),sQuery(id+"F32.wireOp",EDGE,"E31")])]})});
            var Q13;
            Q13=makeQuery(id+"F33.boolean.opBoolean","COPY",EDGE,{"derivedFrom":makeQuery(id+"F33.opExtrude","SWEPT_EDGE",EDGE,{"disambiguationData":[OSD([sQuery(id+"F32.wireOp",EDGE,"E31"),sQuery(id+"F32.wireOp",EDGE,"E32")])]})});
            var Q14;
            Q14=makeQuery(id+"F33.boolean.opBoolean","COPY",EDGE,{"derivedFrom":makeQuery(id+"F33.opExtrude","SWEPT_EDGE",EDGE,{"disambiguationData":[OSD([sQuery(id+"F32.wireOp",EDGE,"E36"),sQuery(id+"F32.wireOp",EDGE,"E37")])]})});
            var Q15;
            Q15=makeQuery(id+"F33.boolean.opBoolean","COPY",EDGE,{"derivedFrom":makeQuery(id+"F33.opExtrude","SWEPT_EDGE",EDGE,{"disambiguationData":[OSD([sQuery(id+"F32.wireOp",EDGE,"E48"),sQuery(id+"F32.wireOp",EDGE,"E49")])]})});
            var Q16;
            Q16=makeQuery(id+"F33.boolean.opBoolean","COPY",EDGE,{"derivedFrom":makeQuery(id+"F33.opExtrude","SWEPT_EDGE",EDGE,{"disambiguationData":[OSD([sQuery(id+"F32.wireOp",EDGE,"E50"),sQuery(id+"F32.wireOp",EDGE,"E51")])]})});
            var Q17;
            Q17=makeQuery(id+"F33.boolean.opBoolean","COPY",EDGE,{"derivedFrom":makeQuery(id+"F33.opExtrude","SWEPT_EDGE",EDGE,{"disambiguationData":[OSD([sQuery(id+"F32.wireOp",EDGE,"E42"),sQuery(id+"F32.wireOp",EDGE,"E43")])]})});
            var Q18;
            Q18=makeQuery(id+"F33.boolean.opBoolean","COPY",EDGE,{"derivedFrom":makeQuery(id+"F33.opExtrude","SWEPT_EDGE",EDGE,{"disambiguationData":[OSD([sQuery(id+"F32.wireOp",EDGE,"E27"),sQuery(id+"F32.wireOp",EDGE,"E34")])]})});
            var Q19;
            Q19=makeQuery(id+"F33.boolean.opBoolean","COPY",EDGE,{"derivedFrom":makeQuery(id+"F33.opExtrude","SWEPT_EDGE",EDGE,{"disambiguationData":[OSD([sQuery(id+"F32.wireOp",EDGE,"E35"),sQuery(id+"F32.wireOp",EDGE,"E46")])]})});
            var Q20;
            Q20=makeQuery(id+"F33.boolean.opBoolean","COPY",EDGE,{"derivedFrom":makeQuery(id+"F33.opExtrude","SWEPT_EDGE",EDGE,{"disambiguationData":[OSD([sQuery(id+"F32.wireOp",EDGE,"E40"),sQuery(id+"F32.wireOp",EDGE,"E41")])]})});
            var Q21;
            Q21=makeQuery(id+"F33.boolean.opBoolean","COPY",EDGE,{"derivedFrom":makeQuery(id+"F33.opExtrude","SWEPT_EDGE",EDGE,{"disambiguationData":[OSD([sQuery(id+"F32.wireOp",EDGE,"E32"),sQuery(id+"F32.wireOp",EDGE,"E33")])]})});
            fillet(context, id + "F34", {"entities" : qUnion([Q0, Q1, Q2, Q3, Q4, Q5, Q6, Q7, Q8, Q9, Q10, Q11, Q12, Q13, Q14, Q15, Q16, Q17, Q18, Q19, Q20, Q21]), "radius" : 4 * mm, "tangentPropagation" : true, "allowEdgeOverflow" : false});
        }
        {
            var Q0;
            Q0=makeQuery(id+"F33.boolean.opBoolean","COPY",EDGE,{"derivedFrom":makeQuery(id+"F33.opExtrude","SWEPT_EDGE",EDGE,{"disambiguationData":[OSD([sQuery(id+"F32.wireOp",EDGE,"E41"),sQuery(id+"F32.wireOp",EDGE,"E42")])]})});
            var Q1;
            Q1=makeQuery(id+"F33.boolean.opBoolean","COPY",EDGE,{"derivedFrom":makeQuery(id+"F33.opExtrude","SWEPT_EDGE",EDGE,{"disambiguationData":[OSD([sQuery(id+"F32.wireOp",EDGE,"E27"),sQuery(id+"F32.wireOp",EDGE,"E28")])]})});
            var Q2;
            Q2=makeQuery(id+"F33.boolean.opBoolean","COPY",EDGE,{"derivedFrom":makeQuery(id+"F33.opExtrude","SWEPT_EDGE",EDGE,{"disambiguationData":[OSD([sQuery(id+"F32.wireOp",EDGE,"E47"),sQuery(id+"F32.wireOp",EDGE,"E48")])]})});
            var Q3;
            Q3=makeQuery(id+"F33.boolean.opBoolean","COPY",EDGE,{"derivedFrom":makeQuery(id+"F33.opExtrude","SWEPT_EDGE",EDGE,{"disambiguationData":[OSD([sQuery(id+"F32.wireOp",EDGE,"E35"),sQuery(id+"F32.wireOp",EDGE,"E36")])]})});
            var Q4;
            Q4=makeQuery(id+"F33.boolean.opBoolean","COPY",EDGE,{"derivedFrom":makeQuery(id+"F33.opExtrude","SWEPT_EDGE",EDGE,{"disambiguationData":[OSD([sQuery(id+"F32.wireOp",EDGE,"E47"),sQuery(id+"F32.wireOp",EDGE,"E54")])]})});
            var Q5;
            Q5=makeQuery(id+"F33.boolean.opBoolean","COPY",EDGE,{"derivedFrom":makeQuery(id+"F33.opExtrude","SWEPT_EDGE",EDGE,{"disambiguationData":[OSD([sQuery(id+"F32.wireOp",EDGE,"E28"),sQuery(id+"F32.wireOp",EDGE,"E29")])]})});
            fillet(context, id + "F35", {"entities" : qUnion([Q0, Q1, Q2, Q3, Q4, Q5]), "radius" : 8 * mm, "tangentPropagation" : true, "allowEdgeOverflow" : false});
        }
    });
